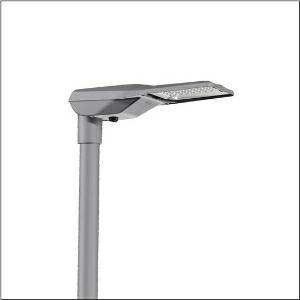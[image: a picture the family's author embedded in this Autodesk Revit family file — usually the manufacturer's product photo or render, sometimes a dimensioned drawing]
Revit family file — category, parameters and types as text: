
# Revit family: streetlight_sl_21_mini___st1_0ab_5xe2m33r08jb_ae43
name_source: partatom
category: Lighting Fixtures
units: mm (PartAtom-declared; Revit-internal decimal feet)

## family parameters
Cut with Voids When Loaded = No
Host = Face
Light Source = No
Part Type = Normal
Room Calculation Point = No
Round Connector Dimension = Use Diameter
Shared = No

## types (1)
- --- (1 x LED, 11390 lm, 88.6 W, 3000K)
    Apparent Load = 89 VA
    CIE Flux Codes = 40 74 97 100 100
    Color Rendering = 70
    Color Temperature = 3000K
    Default Elevation = 1800 mm
    Description = Streetlight SL 21 mini, mast luminaire, primary light control with lens, of PMMA, primary optical cover: cover, of toughened safety glass, transparent, light distribution: ST1.0aB, light emission: direct distribution, primary light characteristic: asymmetric, installation type: side-entry, post-top, LED, High Power LED, rated luminous flux: 11.390lm, luminous efficacy: 129lm/W, light colour: 730, colour temperature: 3000K, control gear: D4i, control: flexible luminous flux parameterisation, time-dependent luminous flux control, constant luminous flux control, overheat protection, pre-setting: logarithmic dimming characteristic, mains connection: 220..240V, AC, 50/60Hz, start of lifetime: 89W, end of service life: 92W, reduction: 41W, luminaire housing, of diecast aluminium, powder-coated, SITECO metallic grey (DB 702S), corrosivity category C5 high according to DIN EN ISO 12944, please order mast flange separately, inclination adjustable: 0°, 5°, 10°, 15°, sealing non-destructively replaceable, multi-level sealing system, length: 628mm, width: 235mm, height: 110mm, mast flange for spigot size: 42mm (side-entry): 5XC10008XM4, 60/48mm (side-entry/post-top): 5XC10108XM2, 76/60mm (side-entry/post-top): 5XC10108XM1, mounting height: 4..8m, Smart Interface below, protection rating (complete): IP66, insulation class (complete): insulation class II (safety insulation), certification: CE, ENEC, ENEC+, VDE, impact resistance: IK10, permissible operating ambient temperature for outdoor applications: -40..+50°C, standard-compliant lighting for roads and squares, packaging unit: 1 piece

Light Distribution: ST1.0aB
    Height = 110 mm
    Lamp = 1 x LED
    Lamp Light Flux = 11390 lm
    Lamp Power = 88.6 W
    Lamp count = 1
    Length = 625 mm
    Luminous efficacy = 129 lm/W
    Manufacturer = Siteco
    ModVariant = No
    Model = 5XE2M33R08JB
    Number of Poles = 1
    OnlyDefault = Yes
    Power Factor = 1
    Product Name = Streetlight SL 21 mini | ST1.0aB
    Product group = mast luminaire | pylon top
    ProductGroupID = 6100
    Protection Class = Protection class II
    Protection Degree = IP 66
    RLX_Detail_Level = 1
    RLX_Emergency_Light_Flux = 0 lm
    RLX_Emergency_Type = 0
    RLX_Emergency_Type_DB = No
    RlxData = <blob elided: 26269 chars, md5=13eac53b>
    Socket = socket
    Standby Power = 0 W
    System Light Flux = 11390 lm
    System Power = 89 W
    Type Comments = factory setting: luminous flux: 100 % | dim-lin: 254 | 915 mA
    Type Image = l_1003516.jpg
    URL = http://relux.com
    VarID = @adj_030551
    Voltage = 0 V
    Weight = 0.00 kg
    Width = 234 mm

## geometry (parser evidence)
native form markers: Blend x4, Sweep x11
no freeform markers — native parametric forms only
